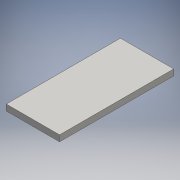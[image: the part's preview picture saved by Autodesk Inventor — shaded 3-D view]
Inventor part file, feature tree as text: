
AUTODESK INVENTOR PART (.ipt)
format: ipt  version: 2016 SP1 (Build 200210100, 210)  size: 88,064 bytes
history: native  units: mm
features: extrude x1, sketch x1
ambient origin geometry x8: Origin, YZ Plane, XZ Plane, XY Plane, X Axis, Y Axis, Z Axis, Center Point
bodies: Solid1 (feature_tree)
feature tree (2):
  extrude  "Extrusion1"  Depth=150.0mm
  sketch  "Sketch1"  dims[d0=70.0mm d1=150.0mm d2=75.0mm d3=35.0mm d4=8.0mm d5=0.0mm]
